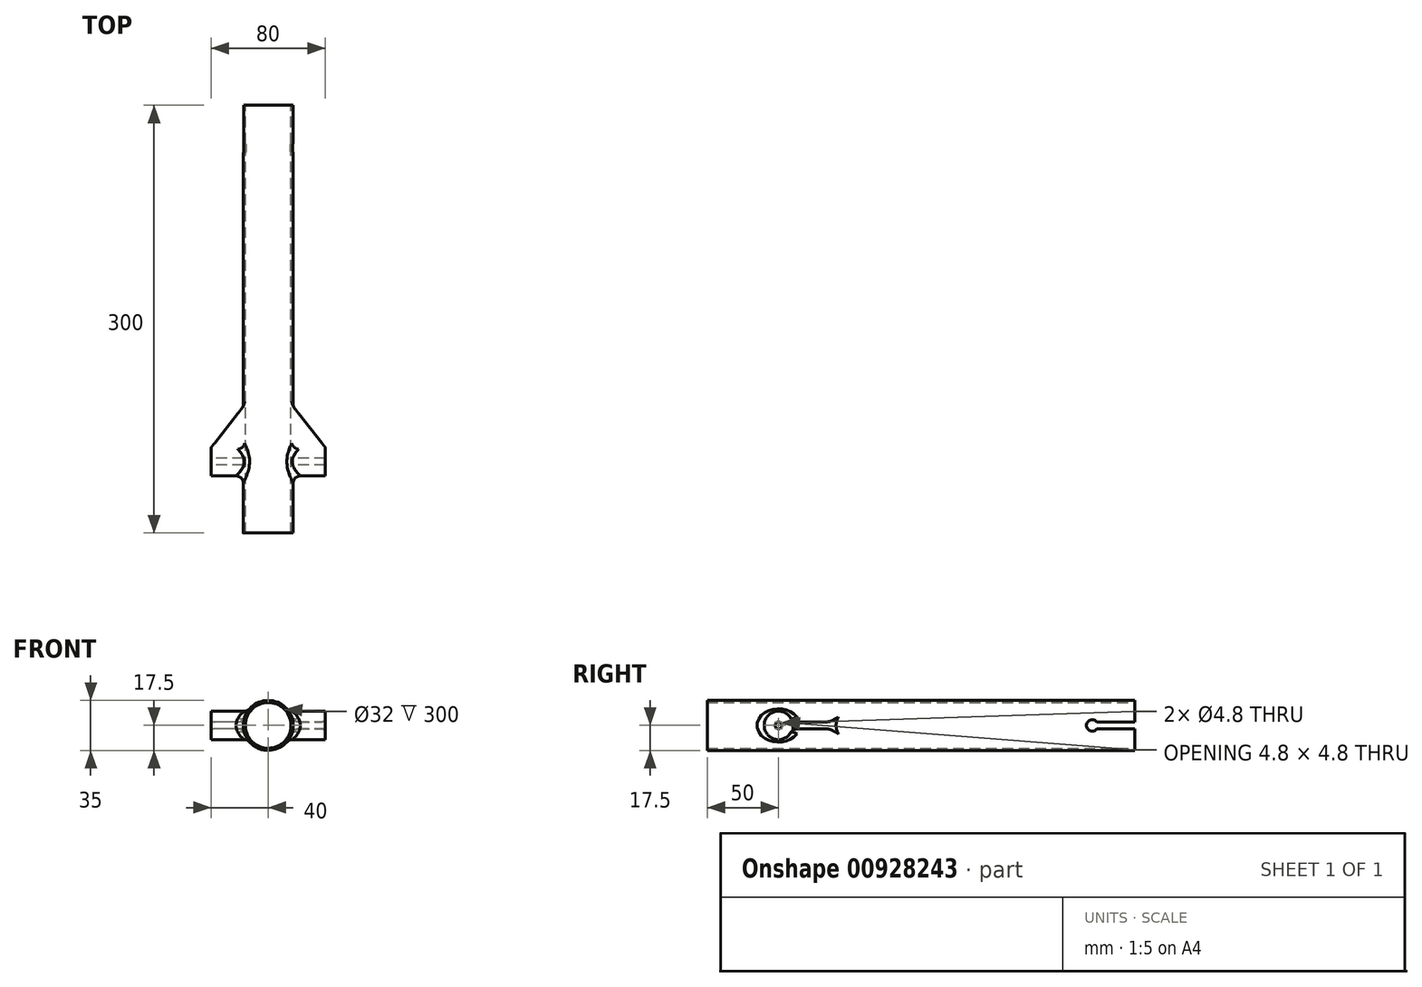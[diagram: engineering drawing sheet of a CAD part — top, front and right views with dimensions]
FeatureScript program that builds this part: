
annotation { "Feature Type Name" : "Feature", "Feature Type Description" : "" }
export const myFeature = defineFeature(function(context is Context, id is Id, definition is map)
    precondition{}
    {
        {
            var Q0;
            Q0=qCreatedBy(makeId("Front.planeOp"),FACE);
            var sketch = newSketch(context, id + "F0", { "sketchPlane" : qUnion([Q0])});
            skCircle(sketch, "E0", {"center": v(0, 0) * mm, "radius": 17.5 * mm});
            skSolve(sketch);
        }
        {
            var Q0;
            Q0=qCreatedBy(makeId("Right.planeOp"),FACE);
            var sketch = newSketch(context, id + "F1", { "sketchPlane" : qUnion([Q0])});
            skCircle(sketch, "E1", {"center": v(-250, 0) * mm, "radius": 10 * mm});
            skSolve(sketch);
        }
        {
            var Q0;
            Q0=qCreatedBy(makeId("Right.planeOp"),FACE);
            var sketch = newSketch(context, id + "F2", { "sketchPlane" : qUnion([Q0])});
            skPoint(sketch, "E2.0", {"position": v(-250, 0) * mm});
            skCircle(sketch, "E3", {"center": v(-250, 0) * mm, "radius": 2.4 * mm});
            skSolve(sketch);
        }
        {
            var Q0;
            Q0=qCreatedBy(makeId("Front.planeOp"),FACE);
            var sketch = newSketch(context, id + "F3", { "sketchPlane" : qUnion([Q0])});
            skCircle(sketch, "E4", {"center": v(0, 0) * mm, "radius": 16 * mm});
            skSolve(sketch);
        }
        {
            var Q0;
            Q0=qCreatedBy(makeId("Right.planeOp"),FACE);
            var sketch = newSketch(context, id + "F4", { "sketchPlane" : qUnion([Q0])});
            skArc(sketch, "E5", {"start": v(-26.88, 2.5) * mm, "mid": v(-34, 0) * mm, "end": v(-26.88, -2.5) * mm});
            skArc(sketch, "E6.0.endCap", {"start": v(10, 2.5) * mm, "mid": v(12.5, 0) * mm, "end": v(10, -2.5) * mm});
            skLineSegment(sketch, "E6.0.left", {"start": v(-26.88, 2.5) * mm, "end": v(10, 2.5) * mm});
            skLineSegment(sketch, "E6.0.right", {"start": v(-26.88, -2.5) * mm, "end": v(10, -2.5) * mm});
            skSolve(sketch);
        }
        {
            var Q0;
            Q0=qCreatedBy(makeId("Top.planeOp"),FACE);
            var sketch = newSketch(context, id + "F5", { "sketchPlane" : qUnion([Q0])});
            skLineSegment(sketch, "E7", {"start": v(-40, -250) * mm, "end": v(40, -250) * mm, "construction": true});
            skLineSegment(sketch, "E8", {"start": v(0, 0) * mm, "end": v(0, -298.58) * mm, "construction": true});
            skLineSegment(sketch, "E9", {"start": v(-40, -241) * mm, "end": v(-16.45, -241) * mm});
            skLineSegment(sketch, "E10", {"start": v(-16.45, -241) * mm, "end": v(-16.45, -210) * mm});
            skLineSegment(sketch, "E11", {"start": v(-16.45, -210) * mm, "end": v(-40, -240) * mm});
            skLineSegment(sketch, "E12", {"start": v(-40, -240) * mm, "end": v(-40, -241) * mm});
            skLineSegment(sketch, "E13.MirrorCS", {"start": v(16.45, -241) * mm, "end": v(16.45, -210) * mm});
            skLineSegment(sketch, "E14.MirrorCS", {"start": v(40, -241) * mm, "end": v(16.45, -241) * mm});
            skLineSegment(sketch, "E15.MirrorCS", {"start": v(16.45, -210) * mm, "end": v(40, -240) * mm});
            skLineSegment(sketch, "E16.MirrorCS", {"start": v(40, -240) * mm, "end": v(40, -241) * mm});
            skSolve(sketch);
        }
        {
            var Q0;
            Q0=qSketchRegion(id+"F1",true);
            extrude(context, id + "F6", {"entities" : qUnion([Q0]), "endBound" : BoundingType.SYMMETRIC, "depth" : 80 * mm, "offsetDistance" : 25 * mm});
        }
        {
            var Q0;
            Q0=qSketchRegion(id+"F2",true);
            extrude(context, id + "F7", {"entities" : qUnion([Q0]), "operationType" : NewBodyOperationType.REMOVE, "endBound" : BoundingType.SYMMETRIC, "depth" : 80 * mm, "offsetDistance" : 25 * mm});
        }
        {
            var Q0;
            Q0=qSketchRegion(id+"F3",true);
            var Q1;
            Q1=qSketchRegion(id+"F0",true);
            extrude(context, id + "F8", {"entities" : qUnion([Q0, Q1]), "operationType" : NewBodyOperationType.ADD, "depth" : 300 * mm, "offsetDistance" : 25 * mm});
        }
        {
            var Q0;
            Q0=qSketchRegion(id+"F3",true);
            extrude(context, id + "F9", {"entities" : qUnion([Q0]), "operationType" : NewBodyOperationType.REMOVE, "depth" : 300 * mm, "offsetDistance" : 25 * mm});
        }
        {
            var Q0;
            Q0=qSketchRegion(id+"F4",true);
            extrude(context, id + "F10", {"entities" : qUnion([Q0]), "operationType" : NewBodyOperationType.REMOVE, "endBound" : BoundingType.SYMMETRIC, "oppositeDirection" : true, "depth" : 50 * mm, "offsetDistance" : 25 * mm});
        }
        {
            var Q0;
            Q0=qSketchRegion(id+"F5",true);
            extrude(context, id + "F11", {"entities" : qUnion([Q0]), "operationType" : NewBodyOperationType.ADD, "endBound" : BoundingType.SYMMETRIC, "depth" : 5 * mm, "offsetDistance" : 25 * mm});
        }
        {
            var Q0;
            {var subQ0=sQuery(id+"F1.wireOp",EDGE,"E1");Q0=makeQuery(id+"F11.boolean.opBoolean","INTERSECT",EDGE,{"derivedFrom":[makeQuery(id+"F8.boolean.opBoolean","SPLIT",FACE,{"disambiguationData":[TD([makeQuery(id+"F6.opExtrude","CAP_FACE",FACE,{"disambiguationData":[OSD([subQ0])],"isStart":false})])],"derivedFrom":makeQuery(id+"F6.opExtrude","SWEPT_FACE",FACE,{"disambiguationData":[OSD([subQ0])]})}),makeQuery(id+"F11.opExtrude","CAP_FACE",FACE,{"disambiguationData":[OSD([sQuery(id+"F5.wireOp",EDGE,"E13.MirrorCS"),sQuery(id+"F5.wireOp",EDGE,"E14.MirrorCS"),sQuery(id+"F5.wireOp",EDGE,"E15.MirrorCS"),sQuery(id+"F5.wireOp",EDGE,"E16.MirrorCS")])],"isStart":false})]});}
            var Q1;
            {var subQ0=sQuery(id+"F0.wireOp",EDGE,"E0");Q1=makeQuery(id+"F11.boolean.opBoolean","INTERSECT",EDGE,{"derivedFrom":[makeQuery(id+"F8.boolean.opBoolean","SPLIT",FACE,{"disambiguationData":[TD([makeQuery(id+"F6.opExtrude","SWEPT_FACE",FACE,{"disambiguationData":[OSD([sQuery(id+"F1.wireOp",EDGE,"E1")])]}),makeQuery(id+"F8.opExtrude","CAP_FACE",FACE,{"disambiguationData":[OSD([subQ0])],"isStart":true}),makeQuery(id+"F8.opExtrude","CAP_FACE",FACE,{"disambiguationData":[OSD([subQ0])],"isStart":false})])],"derivedFrom":makeQuery(id+"F8.opExtrude","SWEPT_FACE",FACE,{"disambiguationData":[OSD([subQ0])]})}),makeQuery(id+"F11.opExtrude","CAP_FACE",FACE,{"disambiguationData":[OSD([sQuery(id+"F5.wireOp",EDGE,"E13.MirrorCS"),sQuery(id+"F5.wireOp",EDGE,"E14.MirrorCS"),sQuery(id+"F5.wireOp",EDGE,"E15.MirrorCS"),sQuery(id+"F5.wireOp",EDGE,"E16.MirrorCS")])],"isStart":false})]});}
            var Q2;
            {var subQ0=makeQuery(id+"F6.opExtrude","SWEPT_FACE",FACE,{"disambiguationData":[OSD([sQuery(id+"F1.wireOp",EDGE,"E1")])]});var subQ1=makeQuery(id+"F8.opExtrude","SWEPT_FACE",FACE,{"disambiguationData":[OSD([sQuery(id+"F0.wireOp",EDGE,"E0")])]});Q2=makeQuery(id+"F11.boolean.opBoolean","SPLIT",EDGE,{"disambiguationData":[TD([makeQuery(id+"F11.opExtrude","CAP_FACE",FACE,{"disambiguationData":[OSD([sQuery(id+"F5.wireOp",EDGE,"E13.MirrorCS"),sQuery(id+"F5.wireOp",EDGE,"E14.MirrorCS"),sQuery(id+"F5.wireOp",EDGE,"E15.MirrorCS"),sQuery(id+"F5.wireOp",EDGE,"E16.MirrorCS")])],"isStart":false})])],"derivedFrom":makeQuery(id+"F8.boolean.opBoolean","INTERSECT",EDGE,{"disambiguationData":[OD(1.0)],"derivedFrom":[subQ0,subQ1]})});}
            var Q3;
            {var subQ0=sQuery(id+"F0.wireOp",EDGE,"E0");Q3=makeQuery(id+"F11.boolean.opBoolean","INTERSECT",EDGE,{"derivedFrom":[makeQuery(id+"F8.boolean.opBoolean","SPLIT",FACE,{"disambiguationData":[TD([makeQuery(id+"F6.opExtrude","SWEPT_FACE",FACE,{"disambiguationData":[OSD([sQuery(id+"F1.wireOp",EDGE,"E1")])]}),makeQuery(id+"F8.opExtrude","CAP_FACE",FACE,{"disambiguationData":[OSD([subQ0])],"isStart":true}),makeQuery(id+"F8.opExtrude","CAP_FACE",FACE,{"disambiguationData":[OSD([subQ0])],"isStart":false})])],"derivedFrom":makeQuery(id+"F8.opExtrude","SWEPT_FACE",FACE,{"disambiguationData":[OSD([subQ0])]})}),makeQuery(id+"F11.opExtrude","CAP_FACE",FACE,{"disambiguationData":[OSD([sQuery(id+"F5.wireOp",EDGE,"5fd8b0b7-ec40-4832-b8a2-6fd4689fd51f1.MirrorCS"),sQuery(id+"F5.wireOp",EDGE,"5fd8b0b7-ec40-4832-b8a2-6fd4689fd51f2.MirrorCS"),sQuery(id+"F5.wireOp",EDGE,"5fd8b0b7-ec40-4832-b8a2-6fd4689fd51f3.MirrorCS"),sQuery(id+"F5.wireOp",EDGE,"5fd8b0b7-ec40-4832-b8a2-6fd4689fd51f7.MirrorCS")])],"isStart":false})]});}
            var Q4;
            {var subQ0=sQuery(id+"F1.wireOp",EDGE,"E1");Q4=makeQuery(id+"F11.boolean.opBoolean","INTERSECT",EDGE,{"derivedFrom":[makeQuery(id+"F8.boolean.opBoolean","SPLIT",FACE,{"disambiguationData":[TD([makeQuery(id+"F6.opExtrude","CAP_FACE",FACE,{"disambiguationData":[OSD([subQ0])],"isStart":false})])],"derivedFrom":makeQuery(id+"F6.opExtrude","SWEPT_FACE",FACE,{"disambiguationData":[OSD([subQ0])]})}),makeQuery(id+"F11.opExtrude","CAP_FACE",FACE,{"disambiguationData":[OSD([sQuery(id+"F5.wireOp",EDGE,"5fd8b0b7-ec40-4832-b8a2-6fd4689fd51f1.MirrorCS"),sQuery(id+"F5.wireOp",EDGE,"5fd8b0b7-ec40-4832-b8a2-6fd4689fd51f2.MirrorCS"),sQuery(id+"F5.wireOp",EDGE,"5fd8b0b7-ec40-4832-b8a2-6fd4689fd51f3.MirrorCS"),sQuery(id+"F5.wireOp",EDGE,"5fd8b0b7-ec40-4832-b8a2-6fd4689fd51f7.MirrorCS")])],"isStart":false})]});}
            var Q5;
            {var subQ0=sQuery(id+"F1.wireOp",EDGE,"E1");Q5=makeQuery(id+"F11.boolean.opBoolean","INTERSECT",EDGE,{"derivedFrom":[makeQuery(id+"F8.boolean.opBoolean","SPLIT",FACE,{"disambiguationData":[TD([makeQuery(id+"F6.opExtrude","CAP_FACE",FACE,{"disambiguationData":[OSD([subQ0])],"isStart":true})])],"derivedFrom":makeQuery(id+"F6.opExtrude","SWEPT_FACE",FACE,{"disambiguationData":[OSD([subQ0])]})}),makeQuery(id+"F11.opExtrude","CAP_FACE",FACE,{"disambiguationData":[OSD([sQuery(id+"F5.wireOp",EDGE,"5fd8b0b7-ec40-4832-b8a2-6fd4689fd51f0.MirrorCS"),sQuery(id+"F5.wireOp",EDGE,"5fd8b0b7-ec40-4832-b8a2-6fd4689fd51f4.MirrorCS"),sQuery(id+"F5.wireOp",EDGE,"5fd8b0b7-ec40-4832-b8a2-6fd4689fd51f5.MirrorCS"),sQuery(id+"F5.wireOp",EDGE,"5fd8b0b7-ec40-4832-b8a2-6fd4689fd51f6.MirrorCS")])],"isStart":false})]});}
            var Q6;
            {var subQ0=makeQuery(id+"F6.opExtrude","SWEPT_FACE",FACE,{"disambiguationData":[OSD([sQuery(id+"F1.wireOp",EDGE,"E1")])]});var subQ1=makeQuery(id+"F8.opExtrude","SWEPT_FACE",FACE,{"disambiguationData":[OSD([sQuery(id+"F0.wireOp",EDGE,"E0")])]});Q6=makeQuery(id+"F11.boolean.opBoolean","SPLIT",EDGE,{"disambiguationData":[TD([makeQuery(id+"F11.opExtrude","CAP_FACE",FACE,{"disambiguationData":[OSD([sQuery(id+"F5.wireOp",EDGE,"E9"),sQuery(id+"F5.wireOp",EDGE,"E10"),sQuery(id+"F5.wireOp",EDGE,"E11"),sQuery(id+"F5.wireOp",EDGE,"E12")])],"isStart":false})])],"derivedFrom":makeQuery(id+"F8.boolean.opBoolean","INTERSECT",EDGE,{"disambiguationData":[OD(0.0)],"derivedFrom":[subQ0,subQ1]})});}
            var Q7;
            {var subQ0=sQuery(id+"F1.wireOp",EDGE,"E1");Q7=makeQuery(id+"F11.boolean.opBoolean","INTERSECT",EDGE,{"derivedFrom":[makeQuery(id+"F8.boolean.opBoolean","SPLIT",FACE,{"disambiguationData":[TD([makeQuery(id+"F6.opExtrude","CAP_FACE",FACE,{"disambiguationData":[OSD([subQ0])],"isStart":true})])],"derivedFrom":makeQuery(id+"F6.opExtrude","SWEPT_FACE",FACE,{"disambiguationData":[OSD([subQ0])]})}),makeQuery(id+"F11.opExtrude","CAP_FACE",FACE,{"disambiguationData":[OSD([sQuery(id+"F5.wireOp",EDGE,"E9"),sQuery(id+"F5.wireOp",EDGE,"E10"),sQuery(id+"F5.wireOp",EDGE,"E11"),sQuery(id+"F5.wireOp",EDGE,"E12")])],"isStart":false})]});}
            var Q8;
            {var subQ0=sQuery(id+"F1.wireOp",EDGE,"E1");Q8=makeQuery(id+"F11.boolean.opBoolean","INTERSECT",EDGE,{"derivedFrom":[makeQuery(id+"F8.boolean.opBoolean","SPLIT",FACE,{"disambiguationData":[TD([makeQuery(id+"F6.opExtrude","CAP_FACE",FACE,{"disambiguationData":[OSD([subQ0])],"isStart":true})])],"derivedFrom":makeQuery(id+"F6.opExtrude","SWEPT_FACE",FACE,{"disambiguationData":[OSD([subQ0])]})}),makeQuery(id+"F11.opExtrude","CAP_FACE",FACE,{"disambiguationData":[OSD([sQuery(id+"F5.wireOp",EDGE,"5fd8b0b7-ec40-4832-b8a2-6fd4689fd51f0.MirrorCS"),sQuery(id+"F5.wireOp",EDGE,"5fd8b0b7-ec40-4832-b8a2-6fd4689fd51f4.MirrorCS"),sQuery(id+"F5.wireOp",EDGE,"5fd8b0b7-ec40-4832-b8a2-6fd4689fd51f5.MirrorCS"),sQuery(id+"F5.wireOp",EDGE,"5fd8b0b7-ec40-4832-b8a2-6fd4689fd51f6.MirrorCS")])],"isStart":true})]});}
            var Q9;
            {var subQ0=makeQuery(id+"F6.opExtrude","SWEPT_FACE",FACE,{"disambiguationData":[OSD([sQuery(id+"F1.wireOp",EDGE,"E1")])]});var subQ1=makeQuery(id+"F8.opExtrude","SWEPT_FACE",FACE,{"disambiguationData":[OSD([sQuery(id+"F0.wireOp",EDGE,"E0")])]});Q9=makeQuery(id+"F11.boolean.opBoolean","SPLIT",EDGE,{"disambiguationData":[TD([makeQuery(id+"F11.opExtrude","CAP_FACE",FACE,{"disambiguationData":[OSD([sQuery(id+"F5.wireOp",EDGE,"E9"),sQuery(id+"F5.wireOp",EDGE,"E10"),sQuery(id+"F5.wireOp",EDGE,"E11"),sQuery(id+"F5.wireOp",EDGE,"E12")])],"isStart":true})])],"derivedFrom":makeQuery(id+"F8.boolean.opBoolean","INTERSECT",EDGE,{"disambiguationData":[OD(0.0)],"derivedFrom":[subQ0,subQ1]})});}
            var Q10;
            {var subQ0=sQuery(id+"F1.wireOp",EDGE,"E1");Q10=makeQuery(id+"F11.boolean.opBoolean","INTERSECT",EDGE,{"derivedFrom":[makeQuery(id+"F8.boolean.opBoolean","SPLIT",FACE,{"disambiguationData":[TD([makeQuery(id+"F6.opExtrude","CAP_FACE",FACE,{"disambiguationData":[OSD([subQ0])],"isStart":true})])],"derivedFrom":makeQuery(id+"F6.opExtrude","SWEPT_FACE",FACE,{"disambiguationData":[OSD([subQ0])]})}),makeQuery(id+"F11.opExtrude","CAP_FACE",FACE,{"disambiguationData":[OSD([sQuery(id+"F5.wireOp",EDGE,"E9"),sQuery(id+"F5.wireOp",EDGE,"E10"),sQuery(id+"F5.wireOp",EDGE,"E11"),sQuery(id+"F5.wireOp",EDGE,"E12")])],"isStart":true})]});}
            var Q11;
            {var subQ0=makeQuery(id+"F6.opExtrude","SWEPT_FACE",FACE,{"disambiguationData":[OSD([sQuery(id+"F1.wireOp",EDGE,"E1")])]});var subQ1=makeQuery(id+"F8.opExtrude","SWEPT_FACE",FACE,{"disambiguationData":[OSD([sQuery(id+"F0.wireOp",EDGE,"E0")])]});Q11=makeQuery(id+"F11.boolean.opBoolean","SPLIT",EDGE,{"disambiguationData":[TD([makeQuery(id+"F11.opExtrude","CAP_FACE",FACE,{"disambiguationData":[OSD([sQuery(id+"F5.wireOp",EDGE,"E13.MirrorCS"),sQuery(id+"F5.wireOp",EDGE,"E14.MirrorCS"),sQuery(id+"F5.wireOp",EDGE,"E15.MirrorCS"),sQuery(id+"F5.wireOp",EDGE,"E16.MirrorCS")])],"isStart":true})])],"derivedFrom":makeQuery(id+"F8.boolean.opBoolean","INTERSECT",EDGE,{"disambiguationData":[OD(1.0)],"derivedFrom":[subQ0,subQ1]})});}
            var Q12;
            {var subQ0=sQuery(id+"F1.wireOp",EDGE,"E1");Q12=makeQuery(id+"F11.boolean.opBoolean","INTERSECT",EDGE,{"derivedFrom":[makeQuery(id+"F8.boolean.opBoolean","SPLIT",FACE,{"disambiguationData":[TD([makeQuery(id+"F6.opExtrude","CAP_FACE",FACE,{"disambiguationData":[OSD([subQ0])],"isStart":false})])],"derivedFrom":makeQuery(id+"F6.opExtrude","SWEPT_FACE",FACE,{"disambiguationData":[OSD([subQ0])]})}),makeQuery(id+"F11.opExtrude","CAP_FACE",FACE,{"disambiguationData":[OSD([sQuery(id+"F5.wireOp",EDGE,"5fd8b0b7-ec40-4832-b8a2-6fd4689fd51f1.MirrorCS"),sQuery(id+"F5.wireOp",EDGE,"5fd8b0b7-ec40-4832-b8a2-6fd4689fd51f2.MirrorCS"),sQuery(id+"F5.wireOp",EDGE,"5fd8b0b7-ec40-4832-b8a2-6fd4689fd51f3.MirrorCS"),sQuery(id+"F5.wireOp",EDGE,"5fd8b0b7-ec40-4832-b8a2-6fd4689fd51f7.MirrorCS")])],"isStart":true})]});}
            var Q13;
            {var subQ0=sQuery(id+"F0.wireOp",EDGE,"E0");Q13=makeQuery(id+"F11.boolean.opBoolean","INTERSECT",EDGE,{"derivedFrom":[makeQuery(id+"F8.boolean.opBoolean","SPLIT",FACE,{"disambiguationData":[TD([makeQuery(id+"F6.opExtrude","SWEPT_FACE",FACE,{"disambiguationData":[OSD([sQuery(id+"F1.wireOp",EDGE,"E1")])]}),makeQuery(id+"F8.opExtrude","CAP_FACE",FACE,{"disambiguationData":[OSD([subQ0])],"isStart":true}),makeQuery(id+"F8.opExtrude","CAP_FACE",FACE,{"disambiguationData":[OSD([subQ0])],"isStart":false})])],"derivedFrom":makeQuery(id+"F8.opExtrude","SWEPT_FACE",FACE,{"disambiguationData":[OSD([subQ0])]})}),makeQuery(id+"F11.opExtrude","CAP_FACE",FACE,{"disambiguationData":[OSD([sQuery(id+"F5.wireOp",EDGE,"5fd8b0b7-ec40-4832-b8a2-6fd4689fd51f1.MirrorCS"),sQuery(id+"F5.wireOp",EDGE,"5fd8b0b7-ec40-4832-b8a2-6fd4689fd51f2.MirrorCS"),sQuery(id+"F5.wireOp",EDGE,"5fd8b0b7-ec40-4832-b8a2-6fd4689fd51f3.MirrorCS"),sQuery(id+"F5.wireOp",EDGE,"5fd8b0b7-ec40-4832-b8a2-6fd4689fd51f7.MirrorCS")])],"isStart":true})]});}
            var Q14;
            {var subQ0=sQuery(id+"F0.wireOp",EDGE,"E0");Q14=makeQuery(id+"F11.boolean.opBoolean","INTERSECT",EDGE,{"derivedFrom":[makeQuery(id+"F8.boolean.opBoolean","SPLIT",FACE,{"disambiguationData":[TD([makeQuery(id+"F6.opExtrude","SWEPT_FACE",FACE,{"disambiguationData":[OSD([sQuery(id+"F1.wireOp",EDGE,"E1")])]}),makeQuery(id+"F8.opExtrude","CAP_FACE",FACE,{"disambiguationData":[OSD([subQ0])],"isStart":true}),makeQuery(id+"F8.opExtrude","CAP_FACE",FACE,{"disambiguationData":[OSD([subQ0])],"isStart":false})])],"derivedFrom":makeQuery(id+"F8.opExtrude","SWEPT_FACE",FACE,{"disambiguationData":[OSD([subQ0])]})}),makeQuery(id+"F11.opExtrude","CAP_FACE",FACE,{"disambiguationData":[OSD([sQuery(id+"F5.wireOp",EDGE,"E13.MirrorCS"),sQuery(id+"F5.wireOp",EDGE,"E14.MirrorCS"),sQuery(id+"F5.wireOp",EDGE,"E15.MirrorCS"),sQuery(id+"F5.wireOp",EDGE,"E16.MirrorCS")])],"isStart":true})]});}
            var Q15;
            {var subQ0=sQuery(id+"F1.wireOp",EDGE,"E1");Q15=makeQuery(id+"F11.boolean.opBoolean","INTERSECT",EDGE,{"derivedFrom":[makeQuery(id+"F8.boolean.opBoolean","SPLIT",FACE,{"disambiguationData":[TD([makeQuery(id+"F6.opExtrude","CAP_FACE",FACE,{"disambiguationData":[OSD([subQ0])],"isStart":false})])],"derivedFrom":makeQuery(id+"F6.opExtrude","SWEPT_FACE",FACE,{"disambiguationData":[OSD([subQ0])]})}),makeQuery(id+"F11.opExtrude","CAP_FACE",FACE,{"disambiguationData":[OSD([sQuery(id+"F5.wireOp",EDGE,"E13.MirrorCS"),sQuery(id+"F5.wireOp",EDGE,"E14.MirrorCS"),sQuery(id+"F5.wireOp",EDGE,"E15.MirrorCS"),sQuery(id+"F5.wireOp",EDGE,"E16.MirrorCS")])],"isStart":true})]});}
            var Q16;
            {var subQ0=sQuery(id+"F0.wireOp",EDGE,"E0");Q16=makeQuery(id+"F11.boolean.opBoolean","INTERSECT",EDGE,{"derivedFrom":[makeQuery(id+"F8.boolean.opBoolean","SPLIT",FACE,{"disambiguationData":[TD([makeQuery(id+"F6.opExtrude","SWEPT_FACE",FACE,{"disambiguationData":[OSD([sQuery(id+"F1.wireOp",EDGE,"E1")])]}),makeQuery(id+"F8.opExtrude","CAP_FACE",FACE,{"disambiguationData":[OSD([subQ0])],"isStart":true}),makeQuery(id+"F8.opExtrude","CAP_FACE",FACE,{"disambiguationData":[OSD([subQ0])],"isStart":false})])],"derivedFrom":makeQuery(id+"F8.opExtrude","SWEPT_FACE",FACE,{"disambiguationData":[OSD([subQ0])]})}),makeQuery(id+"F11.opExtrude","CAP_FACE",FACE,{"disambiguationData":[OSD([sQuery(id+"F5.wireOp",EDGE,"5fd8b0b7-ec40-4832-b8a2-6fd4689fd51f0.MirrorCS"),sQuery(id+"F5.wireOp",EDGE,"5fd8b0b7-ec40-4832-b8a2-6fd4689fd51f4.MirrorCS"),sQuery(id+"F5.wireOp",EDGE,"5fd8b0b7-ec40-4832-b8a2-6fd4689fd51f5.MirrorCS"),sQuery(id+"F5.wireOp",EDGE,"5fd8b0b7-ec40-4832-b8a2-6fd4689fd51f6.MirrorCS")])],"isStart":false})]});}
            var Q17;
            {var subQ0=sQuery(id+"F0.wireOp",EDGE,"E0");Q17=makeQuery(id+"F11.boolean.opBoolean","INTERSECT",EDGE,{"derivedFrom":[makeQuery(id+"F8.boolean.opBoolean","SPLIT",FACE,{"disambiguationData":[TD([makeQuery(id+"F6.opExtrude","SWEPT_FACE",FACE,{"disambiguationData":[OSD([sQuery(id+"F1.wireOp",EDGE,"E1")])]}),makeQuery(id+"F8.opExtrude","CAP_FACE",FACE,{"disambiguationData":[OSD([subQ0])],"isStart":true}),makeQuery(id+"F8.opExtrude","CAP_FACE",FACE,{"disambiguationData":[OSD([subQ0])],"isStart":false})])],"derivedFrom":makeQuery(id+"F8.opExtrude","SWEPT_FACE",FACE,{"disambiguationData":[OSD([subQ0])]})}),makeQuery(id+"F11.opExtrude","CAP_FACE",FACE,{"disambiguationData":[OSD([sQuery(id+"F5.wireOp",EDGE,"E9"),sQuery(id+"F5.wireOp",EDGE,"E10"),sQuery(id+"F5.wireOp",EDGE,"E11"),sQuery(id+"F5.wireOp",EDGE,"E12")])],"isStart":false})]});}
            var Q18;
            {var subQ0=sQuery(id+"F0.wireOp",EDGE,"E0");Q18=makeQuery(id+"F11.boolean.opBoolean","INTERSECT",EDGE,{"derivedFrom":[makeQuery(id+"F8.boolean.opBoolean","SPLIT",FACE,{"disambiguationData":[TD([makeQuery(id+"F6.opExtrude","SWEPT_FACE",FACE,{"disambiguationData":[OSD([sQuery(id+"F1.wireOp",EDGE,"E1")])]}),makeQuery(id+"F8.opExtrude","CAP_FACE",FACE,{"disambiguationData":[OSD([subQ0])],"isStart":true}),makeQuery(id+"F8.opExtrude","CAP_FACE",FACE,{"disambiguationData":[OSD([subQ0])],"isStart":false})])],"derivedFrom":makeQuery(id+"F8.opExtrude","SWEPT_FACE",FACE,{"disambiguationData":[OSD([subQ0])]})}),makeQuery(id+"F11.opExtrude","CAP_FACE",FACE,{"disambiguationData":[OSD([sQuery(id+"F5.wireOp",EDGE,"5fd8b0b7-ec40-4832-b8a2-6fd4689fd51f0.MirrorCS"),sQuery(id+"F5.wireOp",EDGE,"5fd8b0b7-ec40-4832-b8a2-6fd4689fd51f4.MirrorCS"),sQuery(id+"F5.wireOp",EDGE,"5fd8b0b7-ec40-4832-b8a2-6fd4689fd51f5.MirrorCS"),sQuery(id+"F5.wireOp",EDGE,"5fd8b0b7-ec40-4832-b8a2-6fd4689fd51f6.MirrorCS")])],"isStart":true})]});}
            var Q19;
            {var subQ0=sQuery(id+"F0.wireOp",EDGE,"E0");Q19=makeQuery(id+"F11.boolean.opBoolean","INTERSECT",EDGE,{"derivedFrom":[makeQuery(id+"F8.boolean.opBoolean","SPLIT",FACE,{"disambiguationData":[TD([makeQuery(id+"F6.opExtrude","SWEPT_FACE",FACE,{"disambiguationData":[OSD([sQuery(id+"F1.wireOp",EDGE,"E1")])]}),makeQuery(id+"F8.opExtrude","CAP_FACE",FACE,{"disambiguationData":[OSD([subQ0])],"isStart":true}),makeQuery(id+"F8.opExtrude","CAP_FACE",FACE,{"disambiguationData":[OSD([subQ0])],"isStart":false})])],"derivedFrom":makeQuery(id+"F8.opExtrude","SWEPT_FACE",FACE,{"disambiguationData":[OSD([subQ0])]})}),makeQuery(id+"F11.opExtrude","CAP_FACE",FACE,{"disambiguationData":[OSD([sQuery(id+"F5.wireOp",EDGE,"E9"),sQuery(id+"F5.wireOp",EDGE,"E10"),sQuery(id+"F5.wireOp",EDGE,"E11"),sQuery(id+"F5.wireOp",EDGE,"E12")])],"isStart":true})]});}
            fillet(context, id + "F12", {"entities" : qUnion([Q0, Q1, Q2, Q3, Q4, Q5, Q6, Q7, Q8, Q9, Q10, Q11, Q12, Q13, Q14, Q15, Q16, Q17, Q18, Q19]), "radius" : 5 * mm, "tangentPropagation" : true});
        }
    });
